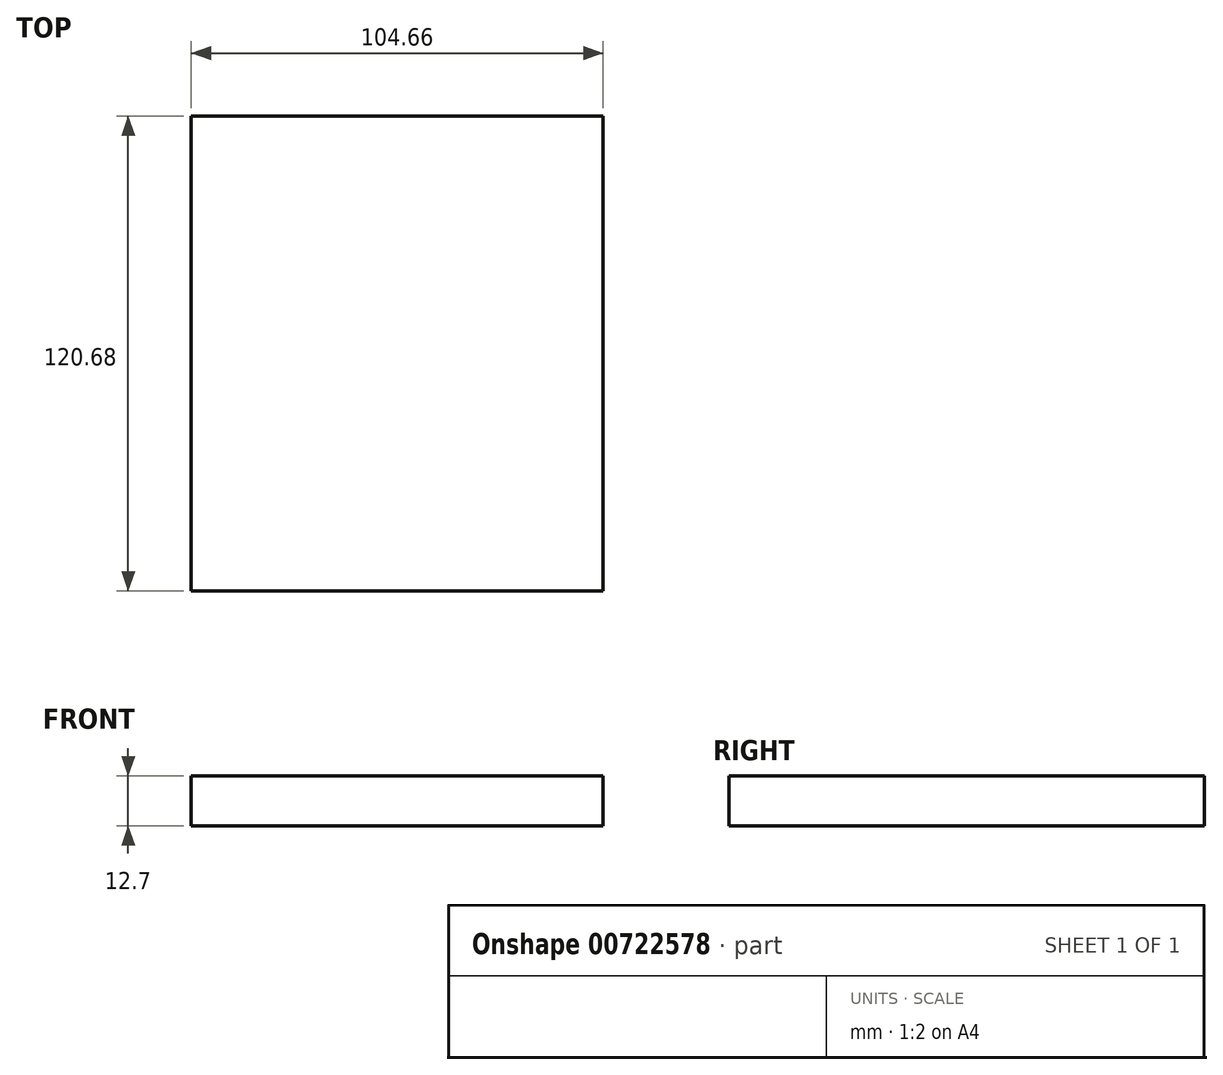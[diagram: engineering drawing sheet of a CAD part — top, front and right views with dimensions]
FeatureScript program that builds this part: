
annotation { "Feature Type Name" : "Feature", "Feature Type Description" : "" }
export const myFeature = defineFeature(function(context is Context, id is Id, definition is map)
    precondition{}
    {
        {
            var Q0;
            Q0=qCreatedBy(makeId("Top.planeOp"),FACE);
            var sketch = newSketch(context, id + "F0", { "sketchPlane" : qUnion([Q0])});
            skLineSegment(sketch, "E0.bottom", {"start": v(52.33, -60.34) * mm, "end": v(-52.33, -60.34) * mm});
            skLineSegment(sketch, "E0.top", {"start": v(52.33, 60.34) * mm, "end": v(-52.33, 60.34) * mm});
            skLineSegment(sketch, "E0.left", {"start": v(52.33, -60.34) * mm, "end": v(52.33, 60.34) * mm});
            skLineSegment(sketch, "E0.right", {"start": v(-52.33, -60.34) * mm, "end": v(-52.33, 60.34) * mm});
            skPoint(sketch, "E0.middle", {"position": v(0, 0) * mm});
            skSolve(sketch);
        }
        {
            var Q0;
            Q0=makeQuery(id+"F0.imprint","IMPRINT",FACE,{"disambiguationData":[TD([[makeQuery(id+"F0.imprint","IMPRINT",EDGE,{"derivedFrom":sQuery(id+"F0.wireOp",EDGE,"E0.bottom")}),-1.0]])]});
            extrude(context, id + "F1", {"entities" : qUnion([Q0]), "depth" : 12.7 * mm, "offsetDistance" : 25.4 * mm});
        }
    });
